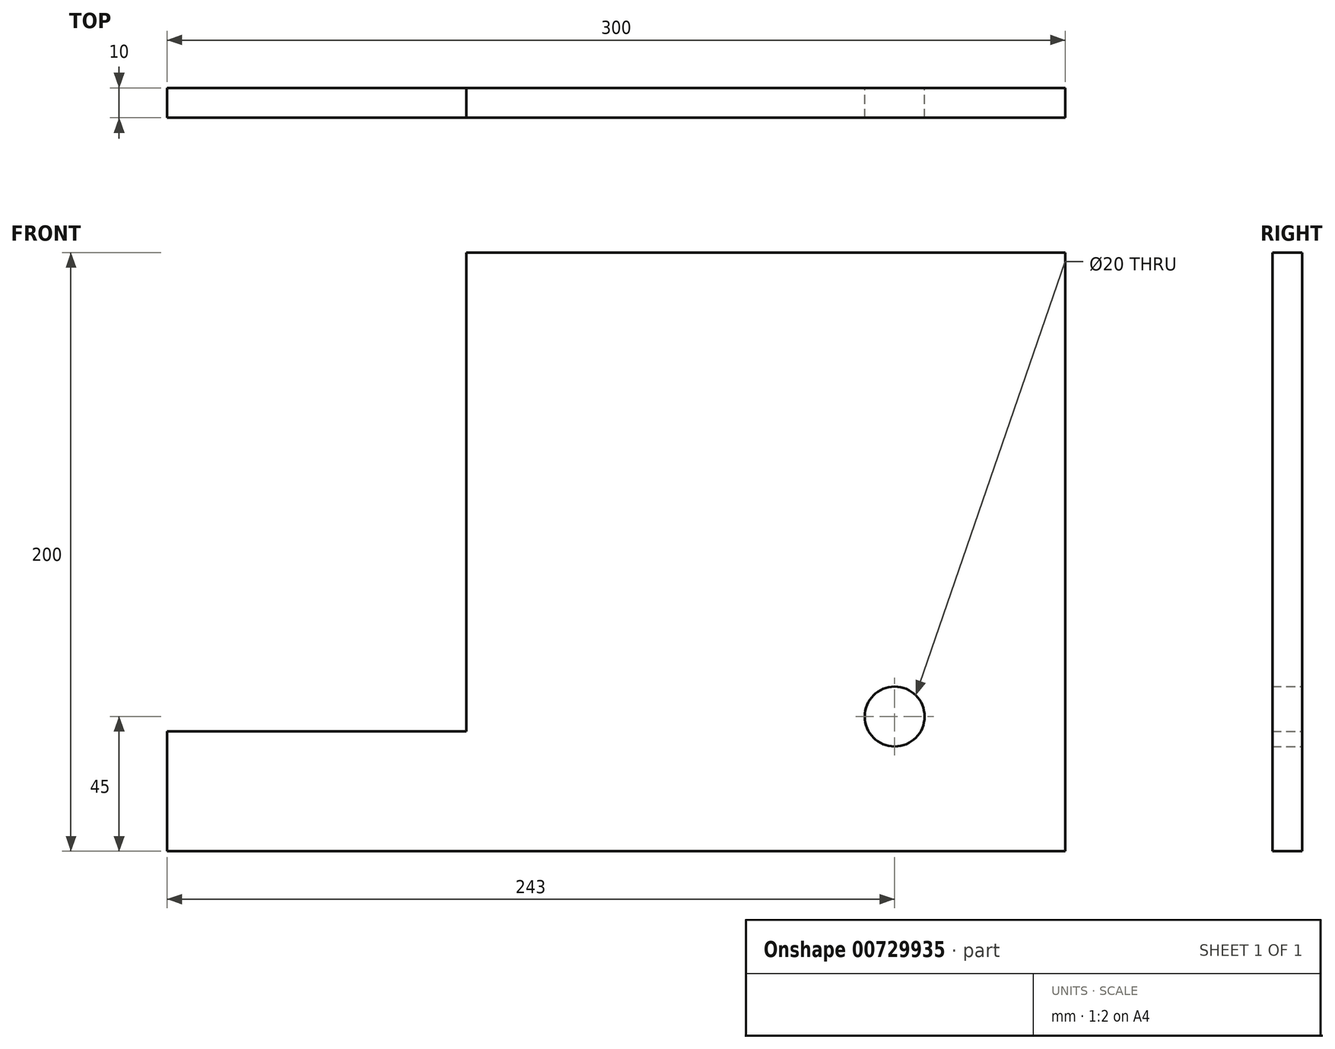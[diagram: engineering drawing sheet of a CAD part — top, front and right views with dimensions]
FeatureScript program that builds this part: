
annotation { "Feature Type Name" : "Feature", "Feature Type Description" : "" }
export const myFeature = defineFeature(function(context is Context, id is Id, definition is map)
    precondition{}
    {
        {
            var Q0;
            Q0=qCreatedBy(makeId("Front.planeOp"),FACE);
            var sketch = newSketch(context, id + "F0", { "sketchPlane" : qUnion([Q0])});
            skLineSegment(sketch, "E0", {"start": v(0, 0) * mm, "end": v(-100, 0) * mm});
            skLineSegment(sketch, "E1", {"start": v(-100, 0) * mm, "end": v(-100, -40) * mm});
            skLineSegment(sketch, "E2", {"start": v(-100, -40) * mm, "end": v(200, -40) * mm});
            skLineSegment(sketch, "E3", {"start": v(200, -40) * mm, "end": v(200, 160) * mm});
            skLineSegment(sketch, "E4", {"start": v(200, 160) * mm, "end": v(0, 160) * mm});
            skLineSegment(sketch, "E5", {"start": v(0, 160) * mm, "end": v(0, 0) * mm});
            skCircle(sketch, "E6", {"center": v(143, 5) * mm, "radius": 10 * mm});
            skSolve(sketch);
        }
        {
            var Q0;
            Q0 = qSketchRegion(id + "F0", true);
            extrude(context, id + "F1", {"entities" : qUnion([Q0]), "depth" : 10 * mm, "offsetDistance" : 25 * mm});
        }
    });
